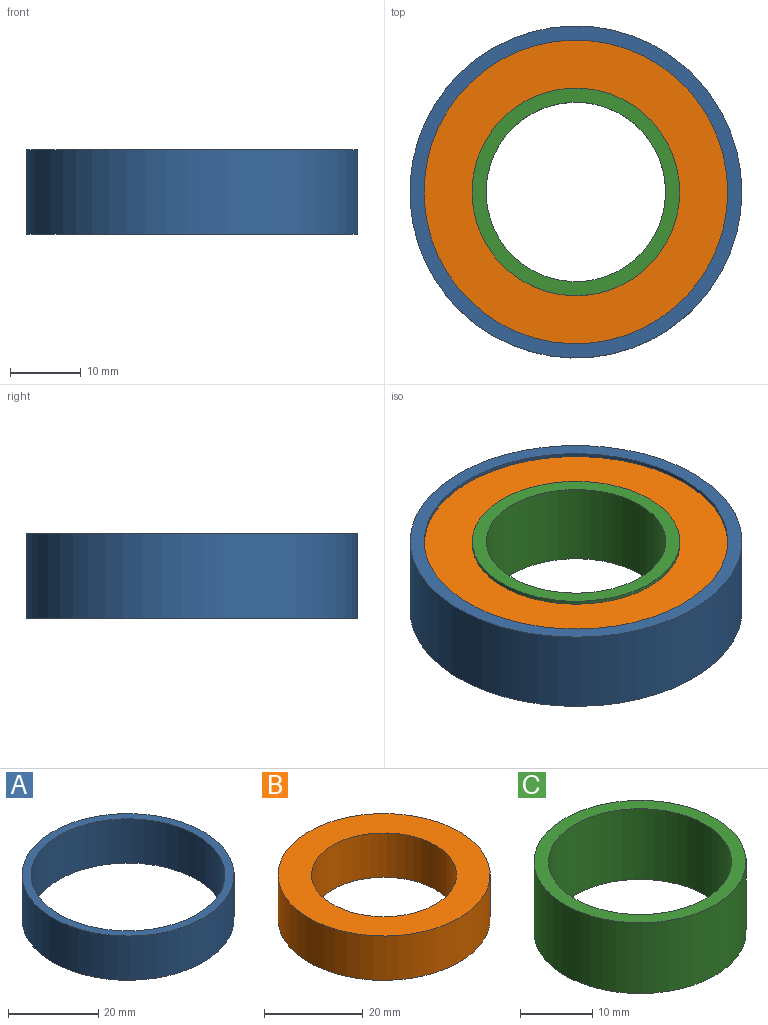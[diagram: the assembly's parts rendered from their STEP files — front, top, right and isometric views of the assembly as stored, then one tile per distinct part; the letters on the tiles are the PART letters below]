
ASSEMBLY  parts=3 mates=2
PART A: 4 faces, bbox 47x47x12 mm
  f0: cylinder r=21.5mm len=43mm, axis (0,0,-1), area 1621.1mm2, adj f2,f3
  f1: cylinder r=23.5mm len=47mm, axis (0,0,-1), area 1771.9mm2, adj f2,f3
  f2: plane 47x47mm, normal (0,0,1), area 282.7mm2, adj f0,f1
  f3: plane 47x47mm, normal (0,0,-1), area 282.7mm2, adj f0,f1
PART B: 4 faces, bbox 43x43x11 mm
  f0: cylinder r=14.7mm len=29.4mm, axis (0,0,-1), area 1016mm2, adj f2,f3
  f1: cylinder r=21.5mm len=43mm, axis (0,0,-1), area 1486mm2, adj f2,f3
  f2: plane 43x43mm, normal (0,0,1), area 773.3mm2, adj f0,f1
  f3: plane 43x43mm, normal (0,0,-1), area 773.3mm2, adj f0,f1
PART C: 4 faces, bbox 29.4x29.4x12 mm
  f0: cylinder r=12.7mm len=25.4mm, axis (0,0,-1), area 957.6mm2, adj f2,f3
  f1: cylinder r=14.7mm len=29.4mm, axis (0,0,-1), area 1108.4mm2, adj f2,f3
  f2: plane 29.4x29.4mm, normal (0,0,1), area 172.2mm2, adj f0,f1
  f3: plane 29.4x29.4mm, normal (0,0,-1), area 172.2mm2, adj f0,f1
PLACE A t=(-17.91,-6.19,6.23)mm
PLACE B t=(-17.91,-6.19,6.23)mm
PLACE C t=(-17.91,-6.19,6.23)mm
MATE fastened B.f0 <-> A.f0  axis (0,0,1) through (-17.91,-6.19,11.73)mm
MATE revolute C.f1 <-> A.f1  axis (0,0,1) through (-17.91,-6.19,12.23)mm
